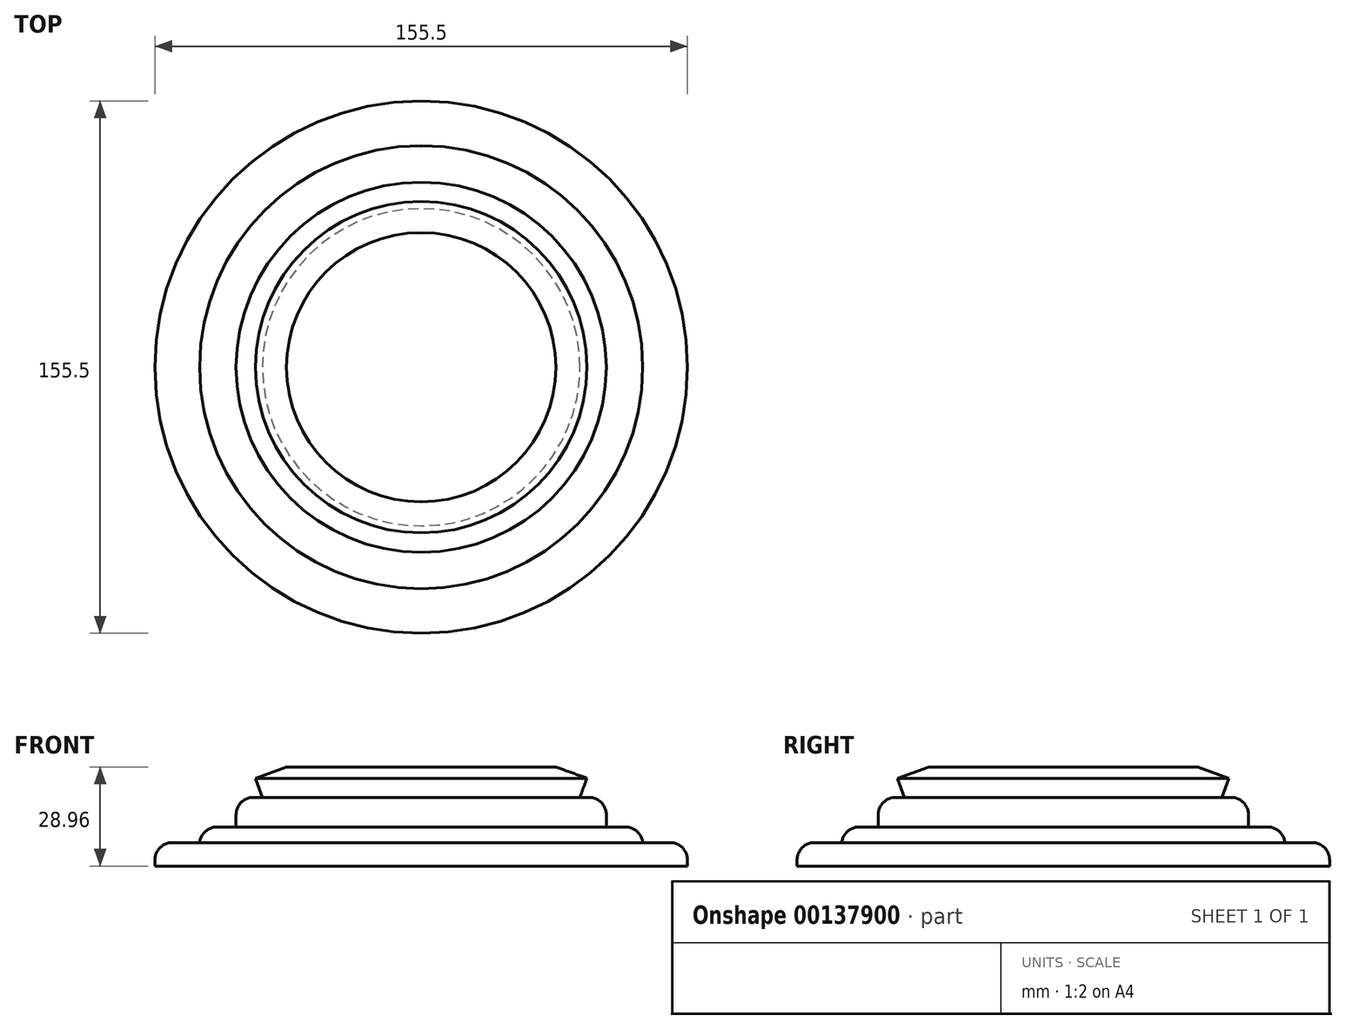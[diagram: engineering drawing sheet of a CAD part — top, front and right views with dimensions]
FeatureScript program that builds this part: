
annotation { "Feature Type Name" : "Feature", "Feature Type Description" : "" }
export const myFeature = defineFeature(function(context is Context, id is Id, definition is map)
    precondition{}
    {
        {
            var Q0;
            Q0=qCreatedBy(makeId("Top.planeOp"),FACE);
            var sketch = newSketch(context, id + "F0", { "sketchPlane" : qUnion([Q0])});
            skCircle(sketch, "E0", {"center": v(0, 0) * mm, "radius": 77.75 * mm});
            skCircle(sketch, "E1", {"center": v(0, 0) * mm, "radius": 64.7 * mm});
            skCircle(sketch, "E2", {"center": v(0, 0) * mm, "radius": 54.05 * mm});
            skCircle(sketch, "E3", {"center": v(0, 0) * mm, "radius": 39.05 * mm});
            skSolve(sketch);
        }
        {
            var Q0;
            Q0=makeQuery(id+"F0.imprint","IMPRINT",FACE,{"disambiguationData":[TD([[makeQuery(id+"F0.imprint","IMPRINT",EDGE,{"derivedFrom":sQuery(id+"F0.wireOp",EDGE,"E0")}),1.0]])]});
            extrude(context, id + "F1", {"entities" : qUnion([Q0]), "depth" : 6.86 * mm});
        }
        {
            var Q0;
            Q0=makeQuery(id+"F0.imprint","IMPRINT",FACE,{"disambiguationData":[TD([[makeQuery(id+"F0.imprint","IMPRINT",EDGE,{"derivedFrom":sQuery(id+"F0.wireOp",EDGE,"E1")}),1.0]])]});
            extrude(context, id + "F2", {"entities" : qUnion([Q0]), "operationType" : NewBodyOperationType.ADD, "depth" : 11.43 * mm});
        }
        {
            var Q0;
            Q0=makeQuery(id+"F0.imprint","IMPRINT",FACE,{"disambiguationData":[TD([[makeQuery(id+"F0.imprint","IMPRINT",EDGE,{"derivedFrom":sQuery(id+"F0.wireOp",EDGE,"E2")}),1.0]])]});
            extrude(context, id + "F3", {"entities" : qUnion([Q0]), "operationType" : NewBodyOperationType.ADD, "depth" : 20.07 * mm});
        }
        {
            var Q0;
            Q0=makeQuery(id+"F3.opExtrude","CAP_EDGE",EDGE,{"disambiguationData":[OSD([sQuery(id+"F0.wireOp",EDGE,"E2")])],"isStart":false});
            var Q1;
            Q1=makeQuery(id+"F2.opExtrude","CAP_EDGE",EDGE,{"disambiguationData":[OSD([sQuery(id+"F0.wireOp",EDGE,"E1")])],"isStart":false});
            var Q2;
            Q2=makeQuery(id+"F1.opExtrude","CAP_EDGE",EDGE,{"disambiguationData":[OSD([sQuery(id+"F0.wireOp",EDGE,"E0")])],"isStart":false});
            fillet(context, id + "F4", {"entities" : qUnion([Q0, Q1, Q2]), "radius" : 5.08 * mm, "tangentPropagation" : true, "allowEdgeOverflow" : false});
        }
        {
            var Q0;
            Q0=makeQuery(id+"F0.imprint","IMPRINT",FACE,{"disambiguationData":[TD([[makeQuery(id+"F0.imprint","IMPRINT",EDGE,{"derivedFrom":sQuery(id+"F0.wireOp",EDGE,"E3")}),1.0]])]});
            extrude(context, id + "F5", {"entities" : qUnion([Q0]), "operationType" : NewBodyOperationType.ADD, "depth" : 25.65 * mm, "hasDraft" : true, "draftAngle" : 20 * degree});
        }
        {
            var Q0;
            Q0=makeQuery(id+"F5.opExtrude","CAP_FACE",FACE,{"disambiguationData":[OSD([sQuery(id+"F0.wireOp",EDGE,"E3")])],"isStart":false});
            extrude(context, id + "F6", {"entities" : qUnion([Q0]), "operationType" : NewBodyOperationType.ADD, "depth" : 3.3 * mm, "hasDraft" : true, "draftAngle" : 70 * degree, "draftPullDirection" : true});
        }
    });
